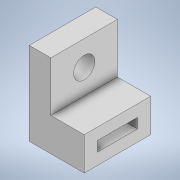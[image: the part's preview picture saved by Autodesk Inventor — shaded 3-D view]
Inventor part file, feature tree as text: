
AUTODESK INVENTOR PART (.ipt)
format: ipt  version: 2020 (Build 240168000, 168)  size: 122,368 bytes
history: native  units: mm
features: extrude x3, sketch x3
ambient origin geometry x8: Origin, YZ Plane, XZ Plane, XY Plane, X Axis, Y Axis, Z Axis, Center Point
bodies: Solid1 (feature_tree)
feature tree (6):
  extrude  "Extrusion1"  Depth=20.0mm
  extrude  "Extrusion2"  Depth=12.0mm
  extrude  "Extrusion3"  Depth=10.0mm
  sketch  "Sketch1"  dims[d0=25.0mm d1=20.0mm]
  sketch  "Sketch2"  dims[d2=3.0mm d3=12.0mm]
  sketch  "Sketch3"  dims[d4=6.5mm d5=0.0mm d6=10.0mm d7=10.0mm d8=0.0mm d9=6.4mm d10=10.0mm d11=0.0mm]
